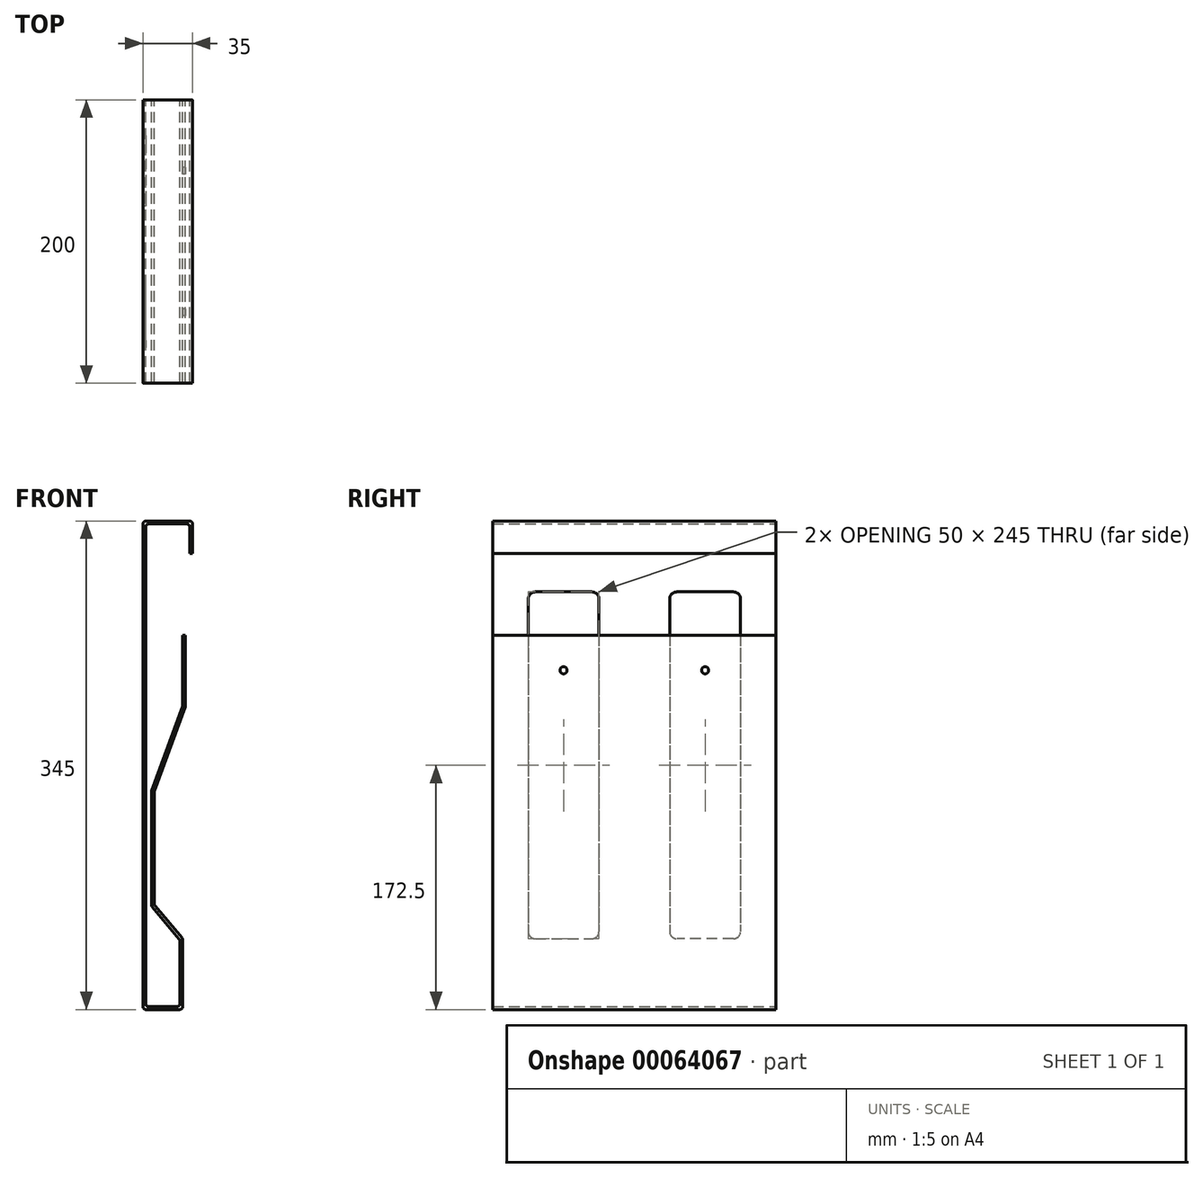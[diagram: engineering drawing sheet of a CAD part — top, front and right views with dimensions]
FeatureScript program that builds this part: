
annotation { "Feature Type Name" : "Feature", "Feature Type Description" : "" }
export const myFeature = defineFeature(function(context is Context, id is Id, definition is map)
    precondition{}
    {
        {
            var Q0;
            Q0=qCreatedBy(makeId("Front.planeOp"),FACE);
            var sketch = newSketch(context, id + "F0", { "sketchPlane" : qUnion([Q0])});
            skLineSegment(sketch, "E0", {"start": v(0, 0) * mm, "end": v(35, 0) * mm});
            skLineSegment(sketch, "E1", {"start": v(35, 0) * mm, "end": v(35, -23) * mm});
            skLineSegment(sketch, "E2", {"start": v(0, 0) * mm, "end": v(0, -345) * mm});
            skLineSegment(sketch, "E3", {"start": v(0, -345) * mm, "end": v(28, -345) * mm});
            skLineSegment(sketch, "E4", {"start": v(28, -295) * mm, "end": v(28, -345) * mm});
            skLineSegment(sketch, "E5.0", {"start": v(33, -2) * mm, "end": v(33, -23) * mm});
            skLineSegment(sketch, "E5.1", {"start": v(26, -295.73) * mm, "end": v(26, -343) * mm});
            skLineSegment(sketch, "E5.2", {"start": v(2, -343) * mm, "end": v(26, -343) * mm});
            skLineSegment(sketch, "E5.3", {"start": v(2, -2) * mm, "end": v(2, -343) * mm});
            skLineSegment(sketch, "E5.4", {"start": v(2, -2) * mm, "end": v(33, -2) * mm});
            skLineSegment(sketch, "E6", {"start": v(33, -23) * mm, "end": v(35, -23) * mm});
            skLineSegment(sketch, "E7", {"start": v(26, -295.73) * mm, "end": v(6, -271.9) * mm});
            skLineSegment(sketch, "E8", {"start": v(6, -271.9) * mm, "end": v(6, -190.81) * mm});
            skLineSegment(sketch, "E9", {"start": v(6, -190.81) * mm, "end": v(28, -130.37) * mm});
            skLineSegment(sketch, "E10", {"start": v(28, -130.37) * mm, "end": v(28, -80.72) * mm});
            skLineSegment(sketch, "E11.0", {"start": v(30, -130.72) * mm, "end": v(30, -80.72) * mm});
            skLineSegment(sketch, "E11.1", {"start": v(8, -191.16) * mm, "end": v(30, -130.72) * mm});
            skLineSegment(sketch, "E11.2", {"start": v(8, -271.16) * mm, "end": v(8, -191.16) * mm});
            skLineSegment(sketch, "E11.3", {"start": v(28, -295) * mm, "end": v(8, -271.16) * mm});
            skLineSegment(sketch, "E12", {"start": v(28, -80.72) * mm, "end": v(30, -80.72) * mm});
            skSolve(sketch);
        }
        {
            var Q0;
            Q0=qSketchRegion(id+"F0",true);
            extrude(context, id + "F1", {"entities" : qUnion([Q0]), "depth" : 200 * mm});
        }
        {
            var Q0;
            Q0=makeQuery(id+"F1.opExtrude","SWEPT_EDGE",EDGE,{"disambiguationData":[OSD([sQuery(id+"F0.wireOp",EDGE,"E0"),sQuery(id+"F0.wireOp",EDGE,"E2")])]});
            var Q1;
            Q1=makeQuery(id+"F1.opExtrude","SWEPT_EDGE",EDGE,{"disambiguationData":[OSD([sQuery(id+"F0.wireOp",EDGE,"E0"),sQuery(id+"F0.wireOp",EDGE,"E1")])]});
            var Q2;
            Q2=makeQuery(id+"F1.opExtrude","SWEPT_EDGE",EDGE,{"disambiguationData":[OSD([sQuery(id+"F0.wireOp",EDGE,"E5.0"),sQuery(id+"F0.wireOp",EDGE,"E5.4")])]});
            var Q3;
            Q3=makeQuery(id+"F1.opExtrude","SWEPT_EDGE",EDGE,{"disambiguationData":[OSD([sQuery(id+"F0.wireOp",EDGE,"E5.3"),sQuery(id+"F0.wireOp",EDGE,"E5.4")])]});
            var Q4;
            Q4=makeQuery(id+"F1.opExtrude","SWEPT_EDGE",EDGE,{"disambiguationData":[OSD([sQuery(id+"F0.wireOp",EDGE,"E2"),sQuery(id+"F0.wireOp",EDGE,"E3")])]});
            var Q5;
            Q5=makeQuery(id+"F1.opExtrude","SWEPT_EDGE",EDGE,{"disambiguationData":[OSD([sQuery(id+"F0.wireOp",EDGE,"E5.2"),sQuery(id+"F0.wireOp",EDGE,"E5.3")])]});
            var Q6;
            Q6=makeQuery(id+"F1.opExtrude","SWEPT_EDGE",EDGE,{"disambiguationData":[OSD([sQuery(id+"F0.wireOp",EDGE,"E3"),sQuery(id+"F0.wireOp",EDGE,"E4")])]});
            var Q7;
            Q7=makeQuery(id+"F1.opExtrude","SWEPT_EDGE",EDGE,{"disambiguationData":[OSD([sQuery(id+"F0.wireOp",EDGE,"E5.1"),sQuery(id+"F0.wireOp",EDGE,"E5.2")])]});
            var Q8;
            Q8=makeQuery(id+"F1.opExtrude","SWEPT_EDGE",EDGE,{"disambiguationData":[OSD([sQuery(id+"F0.wireOp",EDGE,"E5.1"),sQuery(id+"F0.wireOp",EDGE,"E7")])]});
            var Q9;
            Q9=makeQuery(id+"F1.opExtrude","SWEPT_EDGE",EDGE,{"disambiguationData":[OSD([sQuery(id+"F0.wireOp",EDGE,"E4"),sQuery(id+"F0.wireOp",EDGE,"E11.3")])]});
            var Q10;
            Q10=makeQuery(id+"F1.opExtrude","SWEPT_EDGE",EDGE,{"disambiguationData":[OSD([sQuery(id+"F0.wireOp",EDGE,"E11.2"),sQuery(id+"F0.wireOp",EDGE,"E11.3")])]});
            var Q11;
            Q11=makeQuery(id+"F1.opExtrude","SWEPT_EDGE",EDGE,{"disambiguationData":[OSD([sQuery(id+"F0.wireOp",EDGE,"E7"),sQuery(id+"F0.wireOp",EDGE,"E8")])]});
            var Q12;
            Q12=makeQuery(id+"F1.opExtrude","SWEPT_EDGE",EDGE,{"disambiguationData":[OSD([sQuery(id+"F0.wireOp",EDGE,"E8"),sQuery(id+"F0.wireOp",EDGE,"E9")])]});
            var Q13;
            Q13=makeQuery(id+"F1.opExtrude","SWEPT_EDGE",EDGE,{"disambiguationData":[OSD([sQuery(id+"F0.wireOp",EDGE,"E11.1"),sQuery(id+"F0.wireOp",EDGE,"E11.2")])]});
            var Q14;
            Q14=makeQuery(id+"F1.opExtrude","SWEPT_EDGE",EDGE,{"disambiguationData":[OSD([sQuery(id+"F0.wireOp",EDGE,"E11.0"),sQuery(id+"F0.wireOp",EDGE,"E11.1")])]});
            var Q15;
            Q15=makeQuery(id+"F1.opExtrude","SWEPT_EDGE",EDGE,{"disambiguationData":[OSD([sQuery(id+"F0.wireOp",EDGE,"E9"),sQuery(id+"F0.wireOp",EDGE,"E10")])]});
            fillet(context, id + "F2", {"entities" : qUnion([Q0, Q1, Q2, Q3, Q4, Q5, Q6, Q7, Q8, Q9, Q10, Q11, Q12, Q13, Q14, Q15]), "radius" : 2 * mm, "tangentPropagation" : true, "allowEdgeOverflow" : false});
        }
        {
            var Q0;
            Q0=makeQuery(id+"F1.opExtrude","SWEPT_FACE",FACE,{"disambiguationData":[OSD([sQuery(id+"F0.wireOp",EDGE,"E2")])]});
            var sketch = newSketch(context, id + "F3", { "sketchPlane" : qUnion([Q0])});
            skLineSegment(sketch, "E13", {"start": v(100, -2) * mm, "end": v(100, -36.1) * mm, "construction": true});
            skPoint(sketch, "E13.endSnap0", {"position": v(100, -2) * mm});
            skLineSegment(sketch, "E14.bottom", {"start": v(30, -50) * mm, "end": v(70, -50) * mm});
            skLineSegment(sketch, "E14.top", {"start": v(30, -295) * mm, "end": v(70, -295) * mm});
            skLineSegment(sketch, "E14.left", {"start": v(25, -55) * mm, "end": v(25, -290) * mm});
            skLineSegment(sketch, "E14.right", {"start": v(75, -55) * mm, "end": v(75, -290) * mm});
            skPoint(sketch, "E15.visualSharp", {"position": v(25, -50) * mm});
            skArc(sketch, "E15.filletArc", {"start": v(30, -50) * mm, "mid": v(26.46, -51.46) * mm, "end": v(25, -55) * mm});
            skPoint(sketch, "E16.visualSharp", {"position": v(75, -295) * mm});
            skArc(sketch, "E16.filletArc", {"start": v(70, -295) * mm, "mid": v(73.54, -293.54) * mm, "end": v(75, -290) * mm});
            skPoint(sketch, "E17.visualSharp", {"position": v(25, -295) * mm});
            skArc(sketch, "E17.filletArc", {"start": v(25, -290) * mm, "mid": v(26.46, -293.54) * mm, "end": v(30, -295) * mm});
            skPoint(sketch, "E18.visualSharp", {"position": v(75, -50) * mm});
            skArc(sketch, "E18.filletArc", {"start": v(75, -55) * mm, "mid": v(73.54, -51.46) * mm, "end": v(70, -50) * mm});
            skArc(sketch, "E19.MirrorCS", {"start": v(170, -50) * mm, "mid": v(173.54, -51.46) * mm, "end": v(175, -55) * mm});
            skArc(sketch, "E20.MirrorCS", {"start": v(130, -295) * mm, "mid": v(126.46, -293.54) * mm, "end": v(125, -290) * mm});
            skArc(sketch, "E21.MirrorCS", {"start": v(175, -290) * mm, "mid": v(173.54, -293.54) * mm, "end": v(170, -295) * mm});
            skArc(sketch, "E22.MirrorCS", {"start": v(125, -55) * mm, "mid": v(126.46, -51.46) * mm, "end": v(130, -50) * mm});
            skPoint(sketch, "E23.MirrorP", {"position": v(175, -295) * mm});
            skPoint(sketch, "E24.MirrorP", {"position": v(125, -50) * mm});
            skLineSegment(sketch, "E25.MirrorCS", {"start": v(170, -50) * mm, "end": v(130, -50) * mm});
            skLineSegment(sketch, "E26.MirrorCS", {"start": v(170, -295) * mm, "end": v(130, -295) * mm});
            skPoint(sketch, "E27.MirrorP", {"position": v(125, -295) * mm});
            skLineSegment(sketch, "E28.MirrorCS", {"start": v(175, -55) * mm, "end": v(175, -290) * mm});
            skLineSegment(sketch, "E29.MirrorCS", {"start": v(125, -55) * mm, "end": v(125, -290) * mm});
            skPoint(sketch, "E30.MirrorP", {"position": v(175, -50) * mm});
            skSolve(sketch);
        }
        {
            var Q0;
            Q0 = qSketchRegion(id + "F3", true);
            extrude(context, id + "F4", {"entities" : qUnion([Q0]), "operationType" : NewBodyOperationType.REMOVE, "oppositeDirection" : true, "depth" : 2 * mm});
        }
        {
            var Q0;
            Q0=makeQuery(id+"F1.opExtrude","SWEPT_FACE",FACE,{"disambiguationData":[OSD([sQuery(id+"F0.wireOp",EDGE,"E10")])]});
            var sketch = newSketch(context, id + "F5", { "sketchPlane" : qUnion([Q0])});
            skLineSegment(sketch, "E31", {"start": v(0, -105.37) * mm, "end": v(200, -105.37) * mm, "construction": true});
            skPoint(sketch, "E32", {"position": v(50, -105.37) * mm});
            skPoint(sketch, "E33", {"position": v(150, -105.37) * mm});
            skSolve(sketch);
        }
        {
            var Q0;
            Q0=sQuery(id+"F5.wireOp",VERTEX,"E32");
            var Q1;
            Q1=sQuery(id+"F5.wireOp",VERTEX,"E33");
            var Q2;
            Q2=makeQuery(id+"F1.opExtrude","SWEPT_BODY",BODY,{"disambiguationData":[OSD([sQuery(id+"F0.wireOp",EDGE,"E0"),sQuery(id+"F0.wireOp",EDGE,"E1"),sQuery(id+"F0.wireOp",EDGE,"E2"),sQuery(id+"F0.wireOp",EDGE,"E3"),sQuery(id+"F0.wireOp",EDGE,"E4"),sQuery(id+"F0.wireOp",EDGE,"E5.0"),sQuery(id+"F0.wireOp",EDGE,"E5.1"),sQuery(id+"F0.wireOp",EDGE,"E5.2"),sQuery(id+"F0.wireOp",EDGE,"E5.3"),sQuery(id+"F0.wireOp",EDGE,"E5.4"),sQuery(id+"F0.wireOp",EDGE,"E6"),sQuery(id+"F0.wireOp",EDGE,"E7"),sQuery(id+"F0.wireOp",EDGE,"E8"),sQuery(id+"F0.wireOp",EDGE,"E9"),sQuery(id+"F0.wireOp",EDGE,"E10"),sQuery(id+"F0.wireOp",EDGE,"E11.0"),sQuery(id+"F0.wireOp",EDGE,"E11.1"),sQuery(id+"F0.wireOp",EDGE,"E11.2"),sQuery(id+"F0.wireOp",EDGE,"E11.3"),sQuery(id+"F0.wireOp",EDGE,"E12")])]});
            hole(context, id + "F6", {"style" : HoleStyle.SIMPLE, "endStyle" : HoleEndStyle.BLIND, "holeDiameter" : 5 * mm, "holeDepth" : 2 * mm, "locations" : qUnion([Q0, Q1]), "scope" : qUnion([Q2])});
        }
    });
